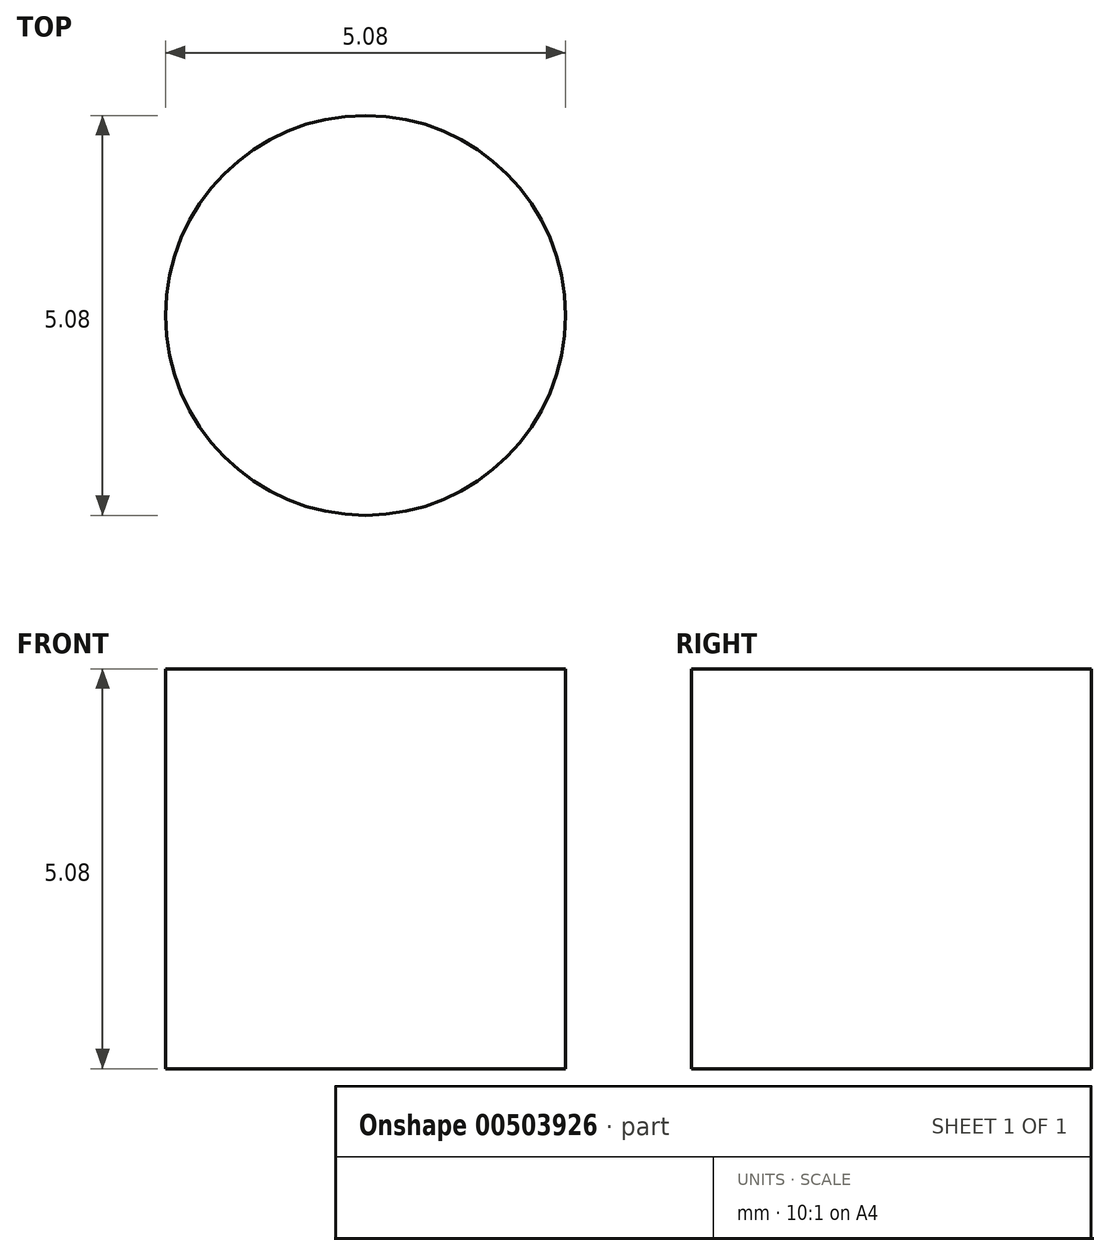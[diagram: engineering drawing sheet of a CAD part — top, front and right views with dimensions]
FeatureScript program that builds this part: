
annotation { "Feature Type Name" : "Feature", "Feature Type Description" : "" }
export const myFeature = defineFeature(function(context is Context, id is Id, definition is map)
    precondition{}
    {
        {
            var Q0;
            Q0=qCreatedBy(makeId("Top.planeOp"),FACE);
            var sketch = newSketch(context, id + "F0", { "sketchPlane" : qUnion([Q0])});
            skCircle(sketch, "E0", {"center": v(0, 0) * mm, "radius": 2.54 * mm});
            skSolve(sketch);
        }
        {
            var Q0;
            Q0=makeQuery(id+"F0.imprint","IMPRINT",FACE,{"disambiguationData":[TD([[makeQuery(id+"F0.imprint","IMPRINT",EDGE,{"derivedFrom":sQuery(id+"F0.wireOp",EDGE,"E0")}),1.0]])]});
            extrude(context, id + "F1", {"entities" : qUnion([Q0]), "depth" : 5.08 * mm});
        }
    });
